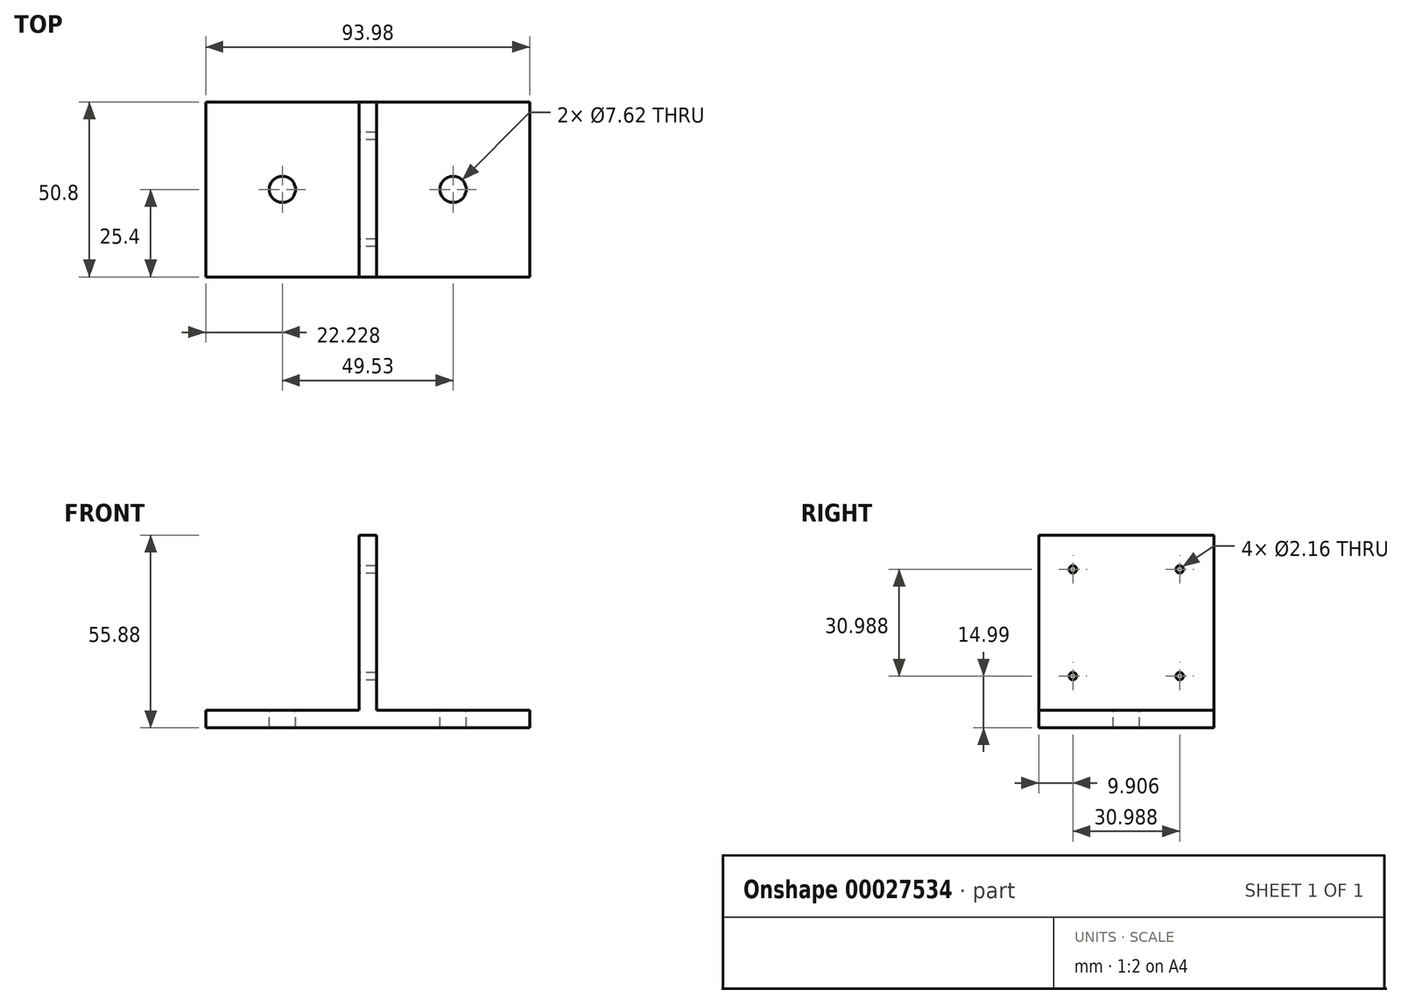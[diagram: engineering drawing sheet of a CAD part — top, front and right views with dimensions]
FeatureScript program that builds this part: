
annotation { "Feature Type Name" : "Feature", "Feature Type Description" : "" }
export const myFeature = defineFeature(function(context is Context, id is Id, definition is map)
    precondition{}
    {
        {
            var Q0;
            Q0=qCreatedBy(makeId("Front.planeOp"),FACE);
            var sketch = newSketch(context, id + "F0", { "sketchPlane" : qUnion([Q0])});
            skLineSegment(sketch, "E0", {"start": v(37.22, -41.86) * mm, "end": v(37.22, -36.78) * mm});
            skLineSegment(sketch, "E1", {"start": v(37.22, -36.78) * mm, "end": v(-7.23, -36.78) * mm});
            skLineSegment(sketch, "E2", {"start": v(-7.23, -36.78) * mm, "end": v(-7.23, 14.02) * mm});
            skLineSegment(sketch, "E3", {"start": v(-7.23, 14.02) * mm, "end": v(-12.3, 14.02) * mm});
            skLineSegment(sketch, "E4", {"start": v(-12.3, 14.02) * mm, "end": v(-12.3, -36.78) * mm});
            skLineSegment(sketch, "E5", {"start": v(-12.3, -36.78) * mm, "end": v(-56.76, -36.78) * mm});
            skLineSegment(sketch, "E6", {"start": v(-56.76, -36.78) * mm, "end": v(-56.76, -41.86) * mm});
            skLineSegment(sketch, "E7", {"start": v(-56.76, -41.86) * mm, "end": v(37.22, -41.86) * mm});
            skSolve(sketch);
        }
        {
            var Q0;
            Q0=makeQuery(id+"F0.imprint","IMPRINT",FACE,{"disambiguationData":[TD([[makeQuery(id+"F0.imprint","IMPRINT",EDGE,{"derivedFrom":sQuery(id+"F0.wireOp",EDGE,"E0")}),1.0]])]});
            extrude(context, id + "F1", {"entities" : qUnion([Q0]), "oppositeDirection" : true, "depth" : 50.8 * mm});
        }
        {
            var Q0;
            Q0=makeQuery(id+"F1.opExtrude","SWEPT_FACE",FACE,{"disambiguationData":[OSD([sQuery(id+"F0.wireOp",EDGE,"E5")])]});
            var sketch = newSketch(context, id + "F2", { "sketchPlane" : qUnion([Q0])});
            skCircle(sketch, "E8", {"center": v(-34.53, 25.4) * mm, "radius": 3.81 * mm});
            skPoint(sketch, "E8.centerSnap0", {"position": v(-34.53, 50.8) * mm});
            skPoint(sketch, "E8.centerSnap1", {"position": v(-56.76, 25.4) * mm});
            skSolve(sketch);
        }
        {
            var Q0;
            Q0=makeQuery(id+"F1.opExtrude","SWEPT_FACE",FACE,{"disambiguationData":[OSD([sQuery(id+"F0.wireOp",EDGE,"E1")])]});
            var sketch = newSketch(context, id + "F3", { "sketchPlane" : qUnion([Q0])});
            skCircle(sketch, "E9", {"center": v(15, 25.4) * mm, "radius": 3.81 * mm});
            skPoint(sketch, "E9.centerSnap0", {"position": v(37.22, 25.4) * mm});
            skPoint(sketch, "E9.centerSnap1", {"position": v(15, 50.8) * mm});
            skSolve(sketch);
        }
        {
            var Q0;
            Q0=sQuery(id+"F3.wireOp",VERTEX,"E9.center");
            var Q1;
            Q1=sQuery(id+"F2.wireOp",VERTEX,"E8.center");
            var Q2;
            Q2=makeQuery(id+"F1.opExtrude","SWEPT_BODY",BODY,{"disambiguationData":[OSD([sQuery(id+"F0.wireOp",EDGE,"E0"),sQuery(id+"F0.wireOp",EDGE,"E1"),sQuery(id+"F0.wireOp",EDGE,"E2"),sQuery(id+"F0.wireOp",EDGE,"E3"),sQuery(id+"F0.wireOp",EDGE,"E4"),sQuery(id+"F0.wireOp",EDGE,"E5"),sQuery(id+"F0.wireOp",EDGE,"E6"),sQuery(id+"F0.wireOp",EDGE,"E7")])]});
            hole(context, id + "F4", {"style" : HoleStyle.SIMPLE, "holeDiameter" : 7.62 * mm, "endStyle" : HoleEndStyle.THROUGH, "locations" : qUnion([Q0, Q1]), "scope" : qUnion([Q2])});
        }
        {
            var Q0;
            Q0=makeQuery(id+"F1.opExtrude","SWEPT_FACE",FACE,{"disambiguationData":[OSD([sQuery(id+"F0.wireOp",EDGE,"E4")])]});
            var sketch = newSketch(context, id + "F5", { "sketchPlane" : qUnion([Q0])});
            skLineSegment(sketch, "E10", {"start": v(-50.8, 14.02) * mm, "end": v(-50.8, 4.12) * mm});
            skLineSegment(sketch, "E11", {"start": v(-50.8, 4.12) * mm, "end": v(-40.9, 4.12) * mm});
            skLineSegment(sketch, "E12", {"start": v(-40.9, 4.12) * mm, "end": v(-40.9, -26.87) * mm});
            skLineSegment(sketch, "E13", {"start": v(-40.9, 4.12) * mm, "end": v(-9.9, 4.12) * mm});
            skLineSegment(sketch, "E14", {"start": v(-9.9, 4.12) * mm, "end": v(-9.9, -26.87) * mm});
            skCircle(sketch, "E15", {"center": v(-40.9, 4.12) * mm, "radius": 1.08 * mm});
            skCircle(sketch, "E16", {"center": v(-9.9, 4.12) * mm, "radius": 1.08 * mm});
            skCircle(sketch, "E17", {"center": v(-9.9, -26.87) * mm, "radius": 1.08 * mm});
            skCircle(sketch, "E18", {"center": v(-40.9, -26.87) * mm, "radius": 1.08 * mm});
            skSolve(sketch);
        }
        {
            var Q0;
            Q0=sQuery(id+"F5.wireOp",VERTEX,"E15.center");
            var Q1;
            Q1=sQuery(id+"F5.wireOp",VERTEX,"E16.center");
            var Q2;
            Q2=sQuery(id+"F5.wireOp",VERTEX,"E17.center");
            var Q3;
            Q3=sQuery(id+"F5.wireOp",VERTEX,"E12.end");
            var Q4;
            Q4=makeQuery(id+"F1.opExtrude","SWEPT_BODY",BODY,{"disambiguationData":[OSD([sQuery(id+"F0.wireOp",EDGE,"E0"),sQuery(id+"F0.wireOp",EDGE,"E1"),sQuery(id+"F0.wireOp",EDGE,"E2"),sQuery(id+"F0.wireOp",EDGE,"E3"),sQuery(id+"F0.wireOp",EDGE,"E4"),sQuery(id+"F0.wireOp",EDGE,"E5"),sQuery(id+"F0.wireOp",EDGE,"E6"),sQuery(id+"F0.wireOp",EDGE,"E7")])]});
            hole(context, id + "F6", {"style" : HoleStyle.SIMPLE, "holeDiameter" : 2.16 * mm, "endStyle" : HoleEndStyle.THROUGH, "locations" : qUnion([Q0, Q1, Q2, Q3]), "scope" : qUnion([Q4])});
        }
    });
